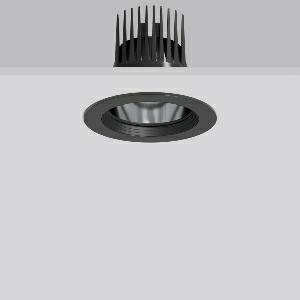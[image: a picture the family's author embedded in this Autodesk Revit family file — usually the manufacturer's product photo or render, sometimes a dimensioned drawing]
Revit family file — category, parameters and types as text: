
# Revit family: heledon_maxi_e_901763_003_1_3727
name_source: partatom
category: Lighting Fixtures
units: mm (PartAtom-declared; Revit-internal decimal feet)

## family parameters
Cut with Voids When Loaded = No
Host = Face
Light Source = No
Part Type = Normal
Room Calculation Point = No
Round Connector Dimension = Use Diameter
Shared = No

## types (1)
- HELEDON maxi E (1 x LED Modul 940, 4400 lm, 4000)
    Apparent Load = 35 VA
    Approval mark = CE
    CIE Flux Codes = 100 100 100 100 100
    Color Rendering = 92
    Color Temperature = 4000
    Default Elevation = 1800 mm
    Description = Series: HELEDON maxi
Round recessed downlight. Housing: die-cast aluminium, powder-coated. Black plastic ring and recessed LED to prevent glare from the side. Optical assembly with reflector made of MIRO-Silver with 98% total light reflection for outstanding efficiency - can be changed without tools. Best colour rendering index Ra>90. Suitable for Recessed ceiling mounting. Installation without tools thanks to spring fastening system. Including separate LED converter with connecting cable 600 mm.High quality converter without flickering and stroboscopic effect. Through-wiring box (5 pole) available as accessory. The following accessories can be mounted without use of tools: interchangeable lenses, decorative glasses, honeycomb louvre, clear and frosted diffusers, white interchangeable plastic ring. 
Colour: deep black, matt (RAL 9005)
Diameter: 162 mm
Height: 3 mm
Cut-out diameter: 152 mm
Recess height: 200 mm
Luminaire: recess height: 135 mm
Lamp: LED
Socket: without socket
Colour temperature: 4000K
Colour rendering index (CRI): 92
System power: 35 W
Rated luminous flux: 4400 lm
Luminous efficiency: 126 lm/W
Control gear: Regulated power supply
Protection class: II
Type of protection: IP 20
    Height = 0 mm  [stored 0 ft]
    Lamp = 1 x LED Modul 940
    Lamp Light Flux = 4400 lm
    Lamp count = 1
    Length = 162 mm
    Lifetime = 50000 h
    Luminous efficacy = 126 lm/W
    Manufacturer = RZB
    ModVariant = No
    Model = 901763.003.1
    Mounting Place = Ceiling
    Mounting Type = Recessed
    Number of Poles = 1
    OnlyDefault = Yes
    Power Factor = 1
    Product Name = HELEDON maxi E
    Product group = Recessed downlights
    ProductGroupID = 402
    Protection Class = Protection class II
    Protection Degree = IP 20
    RLX_Detail_Level = 1
    RLX_Emergency_Light_Flux = 0 lm
    RLX_Emergency_Type = 0
    RLX_Emergency_Type_DB = No
    RlxData = <blob elided: 122561 chars, md5=4ea0fcfb>
    Socket = socket
    Standby Power = 0 W
    System Light Flux = 4400 lm
    System Power = 35 W
    Type Comments = Product without accessories
    Type Image = 901662.003.jpg
    URL = http://relux.com
    VarID = ---
    Voltage = 230 V
    Voltage Range = 220-240 V
    Weight = 0.00 kg
    Width = 0 mm  [stored 0 ft]

note: [stored X ft] marks values corroborated as IEEE doubles in the binary element streams (Revit-internal decimal feet)

## geometry (parser evidence)
native form markers: Blend x4, Sweep x10
no freeform markers — native parametric forms only
